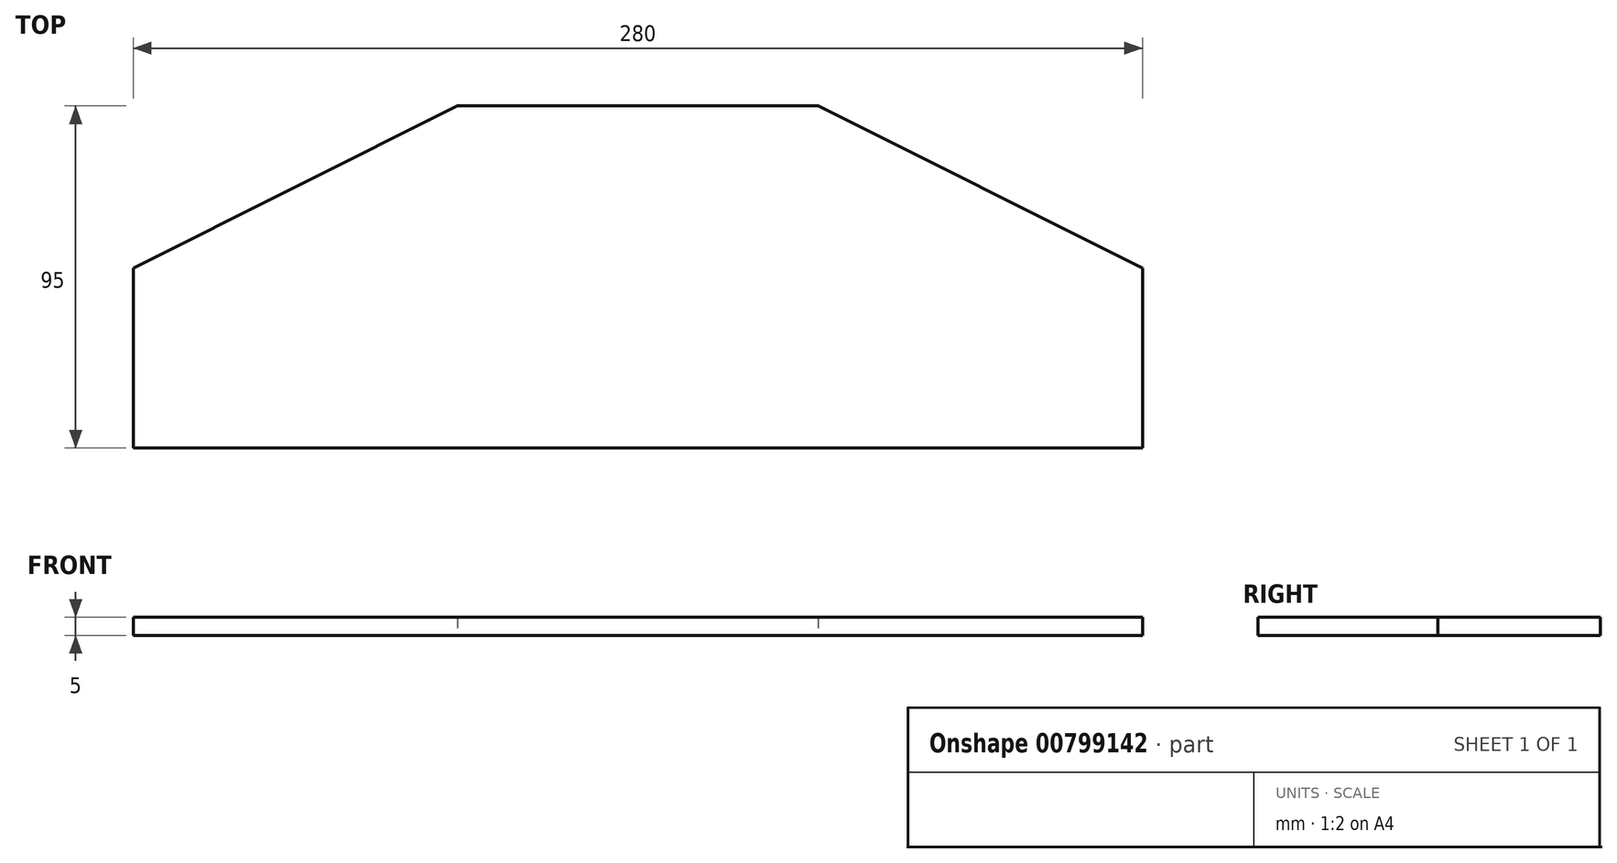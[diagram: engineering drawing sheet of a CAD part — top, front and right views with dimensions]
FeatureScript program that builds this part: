
annotation { "Feature Type Name" : "Feature", "Feature Type Description" : "" }
export const myFeature = defineFeature(function(context is Context, id is Id, definition is map)
    precondition{}
    {
        {
            var Q0;
            Q0=qCreatedBy(makeId("Top.planeOp"),FACE);
            var sketch = newSketch(context, id + "F0", { "sketchPlane" : qUnion([Q0])});
            skLineSegment(sketch, "E0", {"start": v(0, 0) * mm, "end": v(-140, 0) * mm});
            skLineSegment(sketch, "E1", {"start": v(0, 0) * mm, "end": v(140, 0) * mm});
            skLineSegment(sketch, "E2", {"start": v(-140, 0) * mm, "end": v(-140, 50) * mm});
            skLineSegment(sketch, "E3", {"start": v(140, 0) * mm, "end": v(140, 50) * mm});
            skLineSegment(sketch, "E4", {"start": v(0, 0) * mm, "end": v(0, 95) * mm, "construction": true});
            skLineSegment(sketch, "E5", {"start": v(0, 95) * mm, "end": v(-50, 95) * mm});
            skLineSegment(sketch, "E6", {"start": v(0, 95) * mm, "end": v(50, 95) * mm});
            skLineSegment(sketch, "E7", {"start": v(-50, 95) * mm, "end": v(-140, 50) * mm});
            skLineSegment(sketch, "E8", {"start": v(140, 50) * mm, "end": v(50, 95) * mm});
            skSolve(sketch);
        }
        {
            var Q0;
            Q0 = qSketchRegion(id + "F0", true);
            extrude(context, id + "F1", {"entities" : qUnion([Q0]), "endBound" : BoundingType.SYMMETRIC, "depth" : 5 * mm, "offsetDistance" : 25 * mm});
        }
    });
